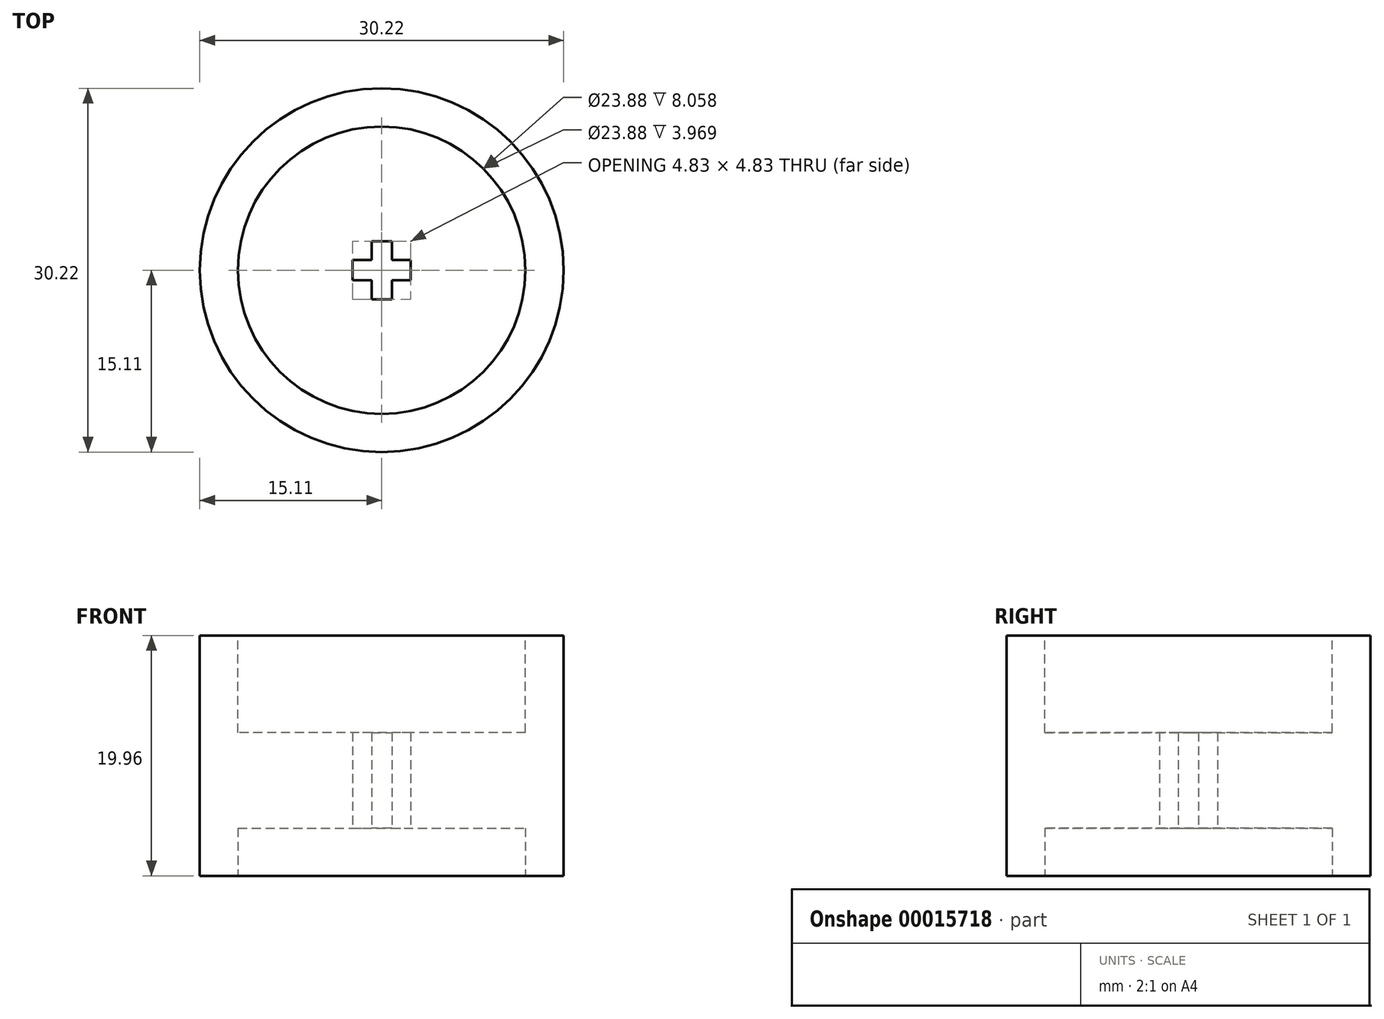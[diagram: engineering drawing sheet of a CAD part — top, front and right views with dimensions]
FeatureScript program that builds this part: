
annotation { "Feature Type Name" : "Feature", "Feature Type Description" : "" }
export const myFeature = defineFeature(function(context is Context, id is Id, definition is map)
    precondition{}
    {
        {
            var Q0;
            Q0=qCreatedBy(makeId("Top.planeOp"),FACE);
            var sketch = newSketch(context, id + "F0", { "sketchPlane" : qUnion([Q0])});
            skCircle(sketch, "E0", {"center": v(0, 0) * mm, "radius": 15.11 * mm});
            skLineSegment(sketch, "E1.rect.bottom", {"start": v(-0.84, 2.41) * mm, "end": v(0.84, 2.41) * mm});
            skLineSegment(sketch, "E1.rect.top", {"start": v(-0.84, -2.41) * mm, "end": v(0.84, -2.41) * mm});
            skLineSegment(sketch, "E1.rect.left", {"start": v(-0.84, 2.41) * mm, "end": v(-0.84, -2.41) * mm});
            skLineSegment(sketch, "E1.rect.right", {"start": v(0.84, 2.41) * mm, "end": v(0.84, -2.41) * mm});
            skLineSegment(sketch, "E2.rect.bottom", {"start": v(2.41, 0.84) * mm, "end": v(-2.41, 0.84) * mm});
            skLineSegment(sketch, "E2.rect.top", {"start": v(2.41, -0.84) * mm, "end": v(-2.41, -0.84) * mm});
            skLineSegment(sketch, "E2.rect.left", {"start": v(2.41, 0.84) * mm, "end": v(2.41, -0.84) * mm});
            skLineSegment(sketch, "E2.rect.right", {"start": v(-2.41, 0.84) * mm, "end": v(-2.41, -0.84) * mm});
            skSolve(sketch);
        }
        {
            var Q0;
            Q0 = qSketchRegion(id + "F0", true);
            extrude(context, id + "F1", {"entities" : qUnion([Q0]), "depth" : 19.96 * mm});
        }
        {
            var Q0;
            Q0=makeQuery(id+"F1.opExtrude","CAP_FACE",FACE,{"disambiguationData":[OSD([sQuery(id+"F0.wireOp",EDGE,"E0"),sQuery(id+"F0.wireOp",EDGE,"E1.rect.bottom"),sQuery(id+"F0.wireOp",EDGE,"E1.rect.top"),sQuery(id+"F0.wireOp",EDGE,"E1.rect.left"),sQuery(id+"F0.wireOp",EDGE,"E1.rect.right"),sQuery(id+"F0.wireOp",EDGE,"E2.rect.bottom"),sQuery(id+"F0.wireOp",EDGE,"E2.rect.top"),sQuery(id+"F0.wireOp",EDGE,"E2.rect.left"),sQuery(id+"F0.wireOp",EDGE,"E2.rect.right")])],"isStart":false});
            var sketch = newSketch(context, id + "F2", { "sketchPlane" : qUnion([Q0])});
            skCircle(sketch, "E3", {"center": v(0, 0) * mm, "radius": 11.94 * mm});
            skSolve(sketch);
        }
        {
            var Q0;
            Q0 = qSketchRegion(id + "F2", true);
            extrude(context, id + "F3", {"entities" : qUnion([Q0]), "operationType" : NewBodyOperationType.REMOVE, "oppositeDirection" : true, "depth" : 8.06 * mm});
        }
        {
            var Q0;
            Q0=makeQuery(id+"F1.opExtrude","CAP_FACE",FACE,{"disambiguationData":[OSD([sQuery(id+"F0.wireOp",EDGE,"E0"),sQuery(id+"F0.wireOp",EDGE,"E1.rect.bottom"),sQuery(id+"F0.wireOp",EDGE,"E1.rect.top"),sQuery(id+"F0.wireOp",EDGE,"E1.rect.left"),sQuery(id+"F0.wireOp",EDGE,"E1.rect.right"),sQuery(id+"F0.wireOp",EDGE,"E2.rect.bottom"),sQuery(id+"F0.wireOp",EDGE,"E2.rect.top"),sQuery(id+"F0.wireOp",EDGE,"E2.rect.left"),sQuery(id+"F0.wireOp",EDGE,"E2.rect.right")])],"isStart":true});
            var sketch = newSketch(context, id + "F4", { "sketchPlane" : qUnion([Q0])});
            skCircle(sketch, "E4", {"center": v(0, 0) * mm, "radius": 11.94 * mm});
            skSolve(sketch);
        }
        {
            var Q0;
            Q0 = qSketchRegion(id + "F4", true);
            extrude(context, id + "F5", {"entities" : qUnion([Q0]), "operationType" : NewBodyOperationType.REMOVE, "oppositeDirection" : true, "depth" : 3.97 * mm});
        }
    });
